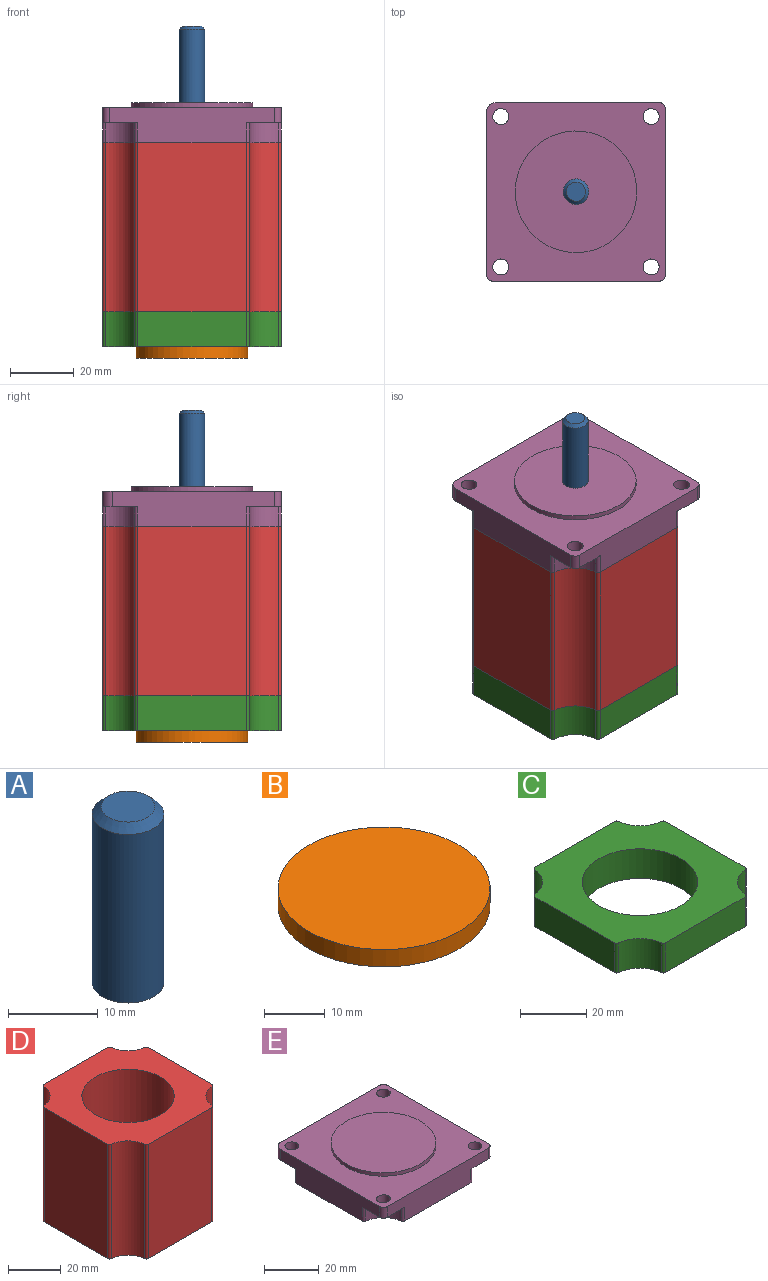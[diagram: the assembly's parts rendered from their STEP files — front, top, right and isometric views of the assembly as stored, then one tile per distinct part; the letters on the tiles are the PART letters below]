
ASSEMBLY  parts=5 mates=4
PART A: 4 faces, bbox 8x8x24 mm
  f0: cylinder r=4mm len=23mm, axis (0,0,-1), area 578.1mm2, adj f2,f3
  f1: plane 6x6mm, normal (0,0,1), area 28.3mm2, adj f3
  f2: plane 8x8mm, normal (0,0,-1), area 50.3mm2, adj f0
  f3: cone r=3mm half-angle=45deg, axis (0,0,-1), area 31.1mm2, adj f0,f1
PART B: 3 faces, bbox 35x35x3.5 mm
  f0: cylinder r=17.5mm len=35mm, axis (0,0,-1), area 384.8mm2, adj f1,f2
  f1: plane 35x35mm, normal (0,0,1), area 962.1mm2, adj f0
  f2: plane 35x35mm, normal (0,0,-1), area 962.1mm2, adj f0
PART C: 19 faces, bbox 56x56x11 mm
  f0: cylinder r=10.04mm len=11mm, axis (0,0,-1), area 153.5mm2, adj f1,f15,f17,f18
  f1: cylinder r=1mm len=11mm, axis (0,0,-1), area 16.3mm2, adj f0,f2,f17,f18
  f2: plane 34x11mm, normal (-1,0,0), area 374mm2, adj f1,f3,f17,f18
  f3: cylinder r=1mm len=11mm, axis (0,0,-1), area 16.3mm2, adj f2,f4,f17,f18
  f4: cylinder r=10.04mm len=11mm, axis (0,0,-1), area 153.5mm2, adj f3,f5,f17,f18
  f5: cylinder r=1mm len=11mm, axis (0,0,-1), area 16.3mm2, adj f4,f6,f17,f18
  f6: plane 34x11mm, normal (0,-1,0), area 374mm2, adj f5,f7,f17,f18
  f7: cylinder r=1mm len=11mm, axis (0,0,-1), area 16.3mm2, adj f6,f8,f17,f18
  f8: cylinder r=10.04mm len=11mm, axis (0,0,-1), area 153.5mm2, adj f7,f9,f17,f18
  f9: cylinder r=1mm len=11mm, axis (0,0,-1), area 16.3mm2, adj f8,f10,f17,f18
  f10: plane 34x11mm, normal (1,0,0), area 374mm2, adj f9,f11,f17,f18
  f11: cylinder r=1mm len=11mm, axis (0,0,-1), area 16.3mm2, adj f10,f12,f17,f18
  f12: cylinder r=10.04mm len=11mm, axis (0,0,-1), area 153.5mm2, adj f11,f13,f17,f18
  f13: cylinder r=1mm len=11mm, axis (0,0,-1), area 16.3mm2, adj f12,f14,f17,f18
  f14: plane 34x11mm, normal (0,1,0), area 374mm2, adj f13,f15,f17,f18
  f15: cylinder r=1mm len=11mm, axis (0,0,-1), area 16.3mm2, adj f0,f14,f17,f18
  f16: cylinder r=17.5mm len=35mm, axis (0,0,-1), area 1209.5mm2, adj f17,f18
  f17: plane 56x56mm, normal (0,0,1), area 1855.3mm2, adj f0,f1,f2,f3,f4,f5,f6,f7
  f18: plane 56x56mm, normal (0,0,-1), area 1855.3mm2, adj f0,f1,f2,f3,f4,f5,f6,f7
PART D: 19 faces, bbox 56x56x53 mm
  f0: cylinder r=10.04mm len=53mm, axis (0,0,-1), area 739.7mm2, adj f1,f15,f17,f18
  f1: cylinder r=1mm len=53mm, axis (0,0,-1), area 78.4mm2, adj f0,f2,f17,f18
  f2: plane 53x34mm, normal (-1,0,0), area 1802mm2, adj f1,f3,f17,f18
  f3: cylinder r=1mm len=53mm, axis (0,0,-1), area 78.4mm2, adj f2,f4,f17,f18
  f4: cylinder r=10.04mm len=53mm, axis (0,0,-1), area 739.7mm2, adj f3,f5,f17,f18
  f5: cylinder r=1mm len=53mm, axis (0,0,-1), area 78.4mm2, adj f4,f6,f17,f18
  f6: plane 53x34mm, normal (0,-1,0), area 1802mm2, adj f5,f7,f17,f18
  f7: cylinder r=1mm len=53mm, axis (0,0,-1), area 78.4mm2, adj f6,f8,f17,f18
  f8: cylinder r=10.04mm len=53mm, axis (0,0,-1), area 739.7mm2, adj f7,f9,f17,f18
  f9: cylinder r=1mm len=53mm, axis (0,0,-1), area 78.4mm2, adj f8,f10,f17,f18
  f10: plane 53x34mm, normal (1,0,0), area 1802mm2, adj f9,f11,f17,f18
  f11: cylinder r=1mm len=53mm, axis (0,0,-1), area 78.4mm2, adj f10,f12,f17,f18
  f12: cylinder r=10.04mm len=53mm, axis (0,0,-1), area 739.7mm2, adj f11,f13,f17,f18
  f13: cylinder r=1mm len=53mm, axis (0,0,-1), area 78.4mm2, adj f12,f14,f17,f18
  f14: plane 53x34mm, normal (0,1,0), area 1802mm2, adj f13,f15,f17,f18
  f15: cylinder r=1mm len=53mm, axis (0,0,-1), area 78.4mm2, adj f0,f14,f17,f18
  f16: cylinder r=17.5mm len=53mm, axis (0,0,-1), area 5827.7mm2, adj f17,f18
  f17: plane 56x56mm, normal (0,0,1), area 1855.3mm2, adj f0,f1,f2,f3,f4,f5,f6,f7
  f18: plane 56x56mm, normal (0,0,-1), area 1855.3mm2, adj f0,f1,f2,f3,f4,f5,f6,f7
PART E: 34 faces, bbox 56x56x12.5 mm
  f0: cylinder r=10.04mm len=9.09mm, axis (0,0,-1), area 86.5mm2, adj f1,f15,f17,f31
  f1: cylinder r=1mm len=6.2mm, axis (0,0,-1), area 9.2mm2, adj f0,f2,f17,f31
  f2: plane 51x11mm, normal (-1,0,0), area 455.6mm2, adj f1,f3,f17,f19,f22,f28,f30,f31
  f3: cylinder r=1mm len=6.2mm, axis (0,0,-1), area 9.2mm2, adj f2,f4,f17,f19
  f4: cylinder r=10.04mm len=9.09mm, axis (0,0,-1), area 86.5mm2, adj f3,f5,f17,f19
  f5: cylinder r=1mm len=6.2mm, axis (0,0,-1), area 9.2mm2, adj f4,f6,f17,f19
  f6: plane 52x11mm, normal (0,-1,0), area 460.4mm2, adj f5,f7,f17,f19,f21,f22,f23,f30
  f7: cylinder r=1mm len=6.2mm, axis (0,0,-1), area 9.2mm2, adj f6,f8,f17,f21
  f8: cylinder r=10.04mm len=9.09mm, axis (0,0,-1), area 86.5mm2, adj f7,f9,f17,f21
  f9: cylinder r=1mm len=6.2mm, axis (0,0,-1), area 9.2mm2, adj f8,f10,f17,f21
  f10: plane 52x11mm, normal (1,0,0), area 460.4mm2, adj f9,f11,f17,f20,f21,f23,f24,f30
  f11: cylinder r=1mm len=6.2mm, axis (0,0,-1), area 9.2mm2, adj f10,f12,f17,f20
  f12: cylinder r=10.04mm len=9.09mm, axis (0,0,-1), area 86.5mm2, adj f11,f13,f17,f20
  f13: cylinder r=1mm len=6.2mm, axis (0,0,-1), area 9.2mm2, adj f12,f14,f17,f20
  f14: plane 51x11mm, normal (0,1,0), area 455.6mm2, adj f13,f15,f17,f20,f24,f28,f30,f31
  f15: cylinder r=1mm len=6.2mm, axis (0,0,-1), area 9.2mm2, adj f0,f14,f17,f31
  f16: cylinder r=17.5mm len=35mm, axis (0,0,-1), area 681.7mm2, adj f17,f18
  f17: plane 56x56mm, normal (0,0,-1), area 1855.3mm2, adj f0,f1,f2,f3,f4,f5,f6,f7
  f18: plane 35x35mm, normal (0,0,-1), area 962.1mm2, adj f16
  f19: plane 11x11mm, normal (0,0,-1), area 59.1mm2, adj f2,f3,f4,f5,f6,f22,f29
  f20: plane 11x11mm, normal (0,0,-1), area 59.1mm2, adj f10,f11,f12,f13,f14,f24,f26
  f21: plane 11x11mm, normal (0,0,-1), area 59.1mm2, adj f6,f7,f8,f9,f10,f23,f25
  f22: cylinder r=2mm len=4.8mm, axis (0,0,-1), area 15.1mm2, adj f2,f6,f19,f30
  f23: cylinder r=2mm len=4.8mm, axis (0,0,-1), area 15.1mm2, adj f6,f10,f21,f30
  f24: cylinder r=2mm len=4.8mm, axis (0,0,-1), area 15.1mm2, adj f10,f14,f20,f30
  f25: cylinder r=2.5mm len=5mm, axis (0,0,-1), area 75.4mm2, adj f21,f30
  f26: cylinder r=2.5mm len=5mm, axis (0,0,-1), area 75.4mm2, adj f20,f30
  f27: cylinder r=2.5mm len=5mm, axis (0,0,-1), area 75.4mm2, adj f30,f31
  f28: cylinder r=3mm len=4.8mm, axis (0,0,-1), area 22.6mm2, adj f2,f14,f30,f31
  f29: cylinder r=2.5mm len=5mm, axis (0,0,-1), area 75.4mm2, adj f19,f30
  f30: plane 56x56mm, normal (0,0,1), area 1912.8mm2, adj f2,f6,f10,f14,f22,f23,f24,f25
  f31: plane 11x11mm, normal (0,0,-1), area 58.1mm2, adj f0,f1,f2,f14,f15,f27,f28
  f32: cylinder r=19.05mm len=38.1mm, axis (0,0,-1), area 179.5mm2, adj f30,f33
  f33: plane 38.1x38.1mm, normal (0,0,1), area 1140.1mm2, adj f32
PLACE A at identity
PLACE B at identity
PLACE C at identity
PLACE D at identity
PLACE E at identity
MATE fastened C.f16 <-> B.f0  axis (0,0,-1) through (0,0,3.5)mm
MATE fastened A.f0 <-> E.f32  axis (0,0,-1) through (0,0,80)mm
MATE fastened E.f16 <-> D.f16  axis (0,0,-1) through (0,0,67.5)mm
MATE fastened D.f16 <-> C.f16  axis (0,0,-1) through (0,0,14.5)mm
